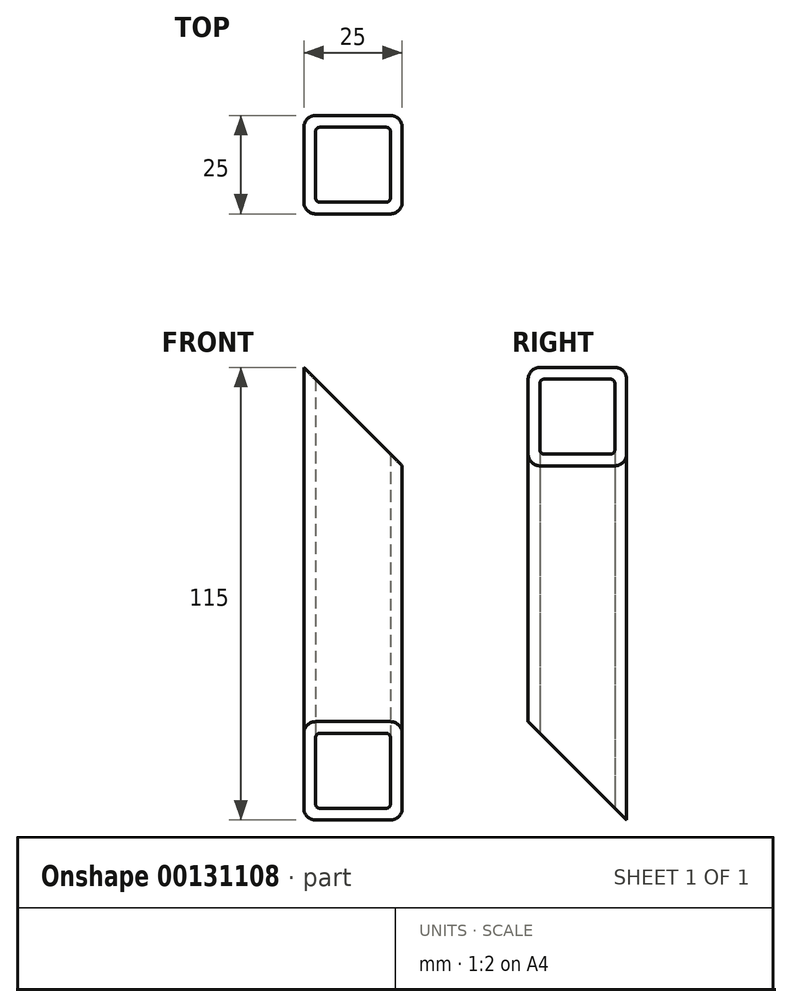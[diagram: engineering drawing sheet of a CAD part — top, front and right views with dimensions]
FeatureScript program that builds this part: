
annotation { "Feature Type Name" : "Feature", "Feature Type Description" : "" }
export const myFeature = defineFeature(function(context is Context, id is Id, definition is map)
    precondition{}
    {
        {
            var Q0;
            Q0=qCreatedBy(makeId("Top.planeOp"),FACE);
            var sketch = newSketch(context, id + "F0", { "sketchPlane" : qUnion([Q0])});
            skLineSegment(sketch, "E0.bottom", {"start": v(12.5, -12.5) * mm, "end": v(-12.5, -12.5) * mm});
            skLineSegment(sketch, "E0.top", {"start": v(12.5, 12.5) * mm, "end": v(-12.5, 12.5) * mm});
            skLineSegment(sketch, "E0.left", {"start": v(12.5, -12.5) * mm, "end": v(12.5, 12.5) * mm});
            skLineSegment(sketch, "E0.right", {"start": v(-12.5, -12.5) * mm, "end": v(-12.5, 12.5) * mm});
            skPoint(sketch, "E0.middle", {"position": v(0, 0) * mm});
            skLineSegment(sketch, "E1.bottom", {"start": v(9.5, -9.5) * mm, "end": v(-9.5, -9.5) * mm});
            skLineSegment(sketch, "E1.top", {"start": v(9.5, 9.5) * mm, "end": v(-9.5, 9.5) * mm});
            skLineSegment(sketch, "E1.left", {"start": v(9.5, -9.5) * mm, "end": v(9.5, 9.5) * mm});
            skLineSegment(sketch, "E1.right", {"start": v(-9.5, -9.5) * mm, "end": v(-9.5, 9.5) * mm});
            skSolve(sketch);
        }
        {
            var Q0;
            Q0=makeQuery(id+"F0.imprint","IMPRINT",FACE,{"disambiguationData":[TD([[makeQuery(id+"F0.imprint","IMPRINT",EDGE,{"derivedFrom":sQuery(id+"F0.wireOp",EDGE,"E0.bottom")}),-1.0]])]});
            extrude(context, id + "F1", {"entities" : qUnion([Q0]), "depth" : 120 * mm});
        }
        {
            var Q0;
            Q0=makeQuery(id+"F1.opExtrude","SWEPT_EDGE",EDGE,{"disambiguationData":[OSD([sQuery(id+"F0.wireOp",EDGE,"E1.bottom"),sQuery(id+"F0.wireOp",EDGE,"E1.right")])]});
            var Q1;
            Q1=makeQuery(id+"F1.opExtrude","SWEPT_EDGE",EDGE,{"disambiguationData":[OSD([sQuery(id+"F0.wireOp",EDGE,"E1.top"),sQuery(id+"F0.wireOp",EDGE,"E1.right")])]});
            var Q2;
            Q2=makeQuery(id+"F1.opExtrude","SWEPT_EDGE",EDGE,{"disambiguationData":[OSD([sQuery(id+"F0.wireOp",EDGE,"E1.top"),sQuery(id+"F0.wireOp",EDGE,"E1.left")])]});
            var Q3;
            Q3=makeQuery(id+"F1.opExtrude","SWEPT_EDGE",EDGE,{"disambiguationData":[OSD([sQuery(id+"F0.wireOp",EDGE,"E1.bottom"),sQuery(id+"F0.wireOp",EDGE,"E1.left")])]});
            fillet(context, id + "F2", {"entities" : qUnion([Q0, Q1, Q2, Q3]), "radius" : 1 * mm, "tangentPropagation" : true, "allowEdgeOverflow" : false});
        }
        {
            var Q0;
            Q0=makeQuery(id+"F1.opExtrude","SWEPT_EDGE",EDGE,{"disambiguationData":[OSD([sQuery(id+"F0.wireOp",EDGE,"E0.top"),sQuery(id+"F0.wireOp",EDGE,"E0.right")])]});
            var Q1;
            Q1=makeQuery(id+"F1.opExtrude","SWEPT_EDGE",EDGE,{"disambiguationData":[OSD([sQuery(id+"F0.wireOp",EDGE,"E0.bottom"),sQuery(id+"F0.wireOp",EDGE,"E0.right")])]});
            var Q2;
            Q2=makeQuery(id+"F1.opExtrude","SWEPT_EDGE",EDGE,{"disambiguationData":[OSD([sQuery(id+"F0.wireOp",EDGE,"E0.top"),sQuery(id+"F0.wireOp",EDGE,"E0.left")])]});
            var Q3;
            Q3=makeQuery(id+"F1.opExtrude","SWEPT_EDGE",EDGE,{"disambiguationData":[OSD([sQuery(id+"F0.wireOp",EDGE,"E0.bottom"),sQuery(id+"F0.wireOp",EDGE,"E0.left")])]});
            fillet(context, id + "F3", {"entities" : qUnion([Q0, Q1, Q2, Q3]), "radius" : 3 * mm, "tangentPropagation" : true, "allowEdgeOverflow" : false});
        }
        {
            var Q0;
            Q0=makeQuery(id+"F1.opExtrude","SWEPT_FACE",FACE,{"disambiguationData":[OSD([sQuery(id+"F0.wireOp",EDGE,"E0.bottom")])]});
            var sketch = newSketch(context, id + "F4", { "sketchPlane" : qUnion([Q0])});
            skLineSegment(sketch, "E2", {"start": v(-15, 120) * mm, "end": v(15, 90) * mm});
            skPoint(sketch, "E2.startSnap0", {"position": v(0, 120) * mm});
            skLineSegment(sketch, "E3", {"start": v(15, 90) * mm, "end": v(15, 120) * mm});
            skLineSegment(sketch, "E4", {"start": v(-15, 120) * mm, "end": v(15, 120) * mm});
            skSolve(sketch);
        }
        {
            var Q0;
            {var subQ0=sQuery(id+"F4.wireOp",EDGE,"E2");var subQ1=sQuery(id+"F0.wireOp",EDGE,"E0.bottom");var subQ2=makeQuery(id+"F1.opExtrude","SWEPT_FACE",FACE,{"disambiguationData":[OSD([subQ1])]});var subQ3=makeQuery(id+"F3.opFillet","BLEND_EDGE",EDGE,{"blendedFrom":[makeQuery(id+"F1.opExtrude","SWEPT_EDGE",EDGE,{"disambiguationData":[OSD([subQ1,sQuery(id+"F0.wireOp",EDGE,"E0.right")])]}),subQ2],"blendedInto":[subQ2]});var subQ4=makeQuery(id+"F4.imprint","INTERSECT",VERTEX,{"derivedFrom":[subQ3,subQ0]});Q0=makeQuery(id+"F4.imprint","IMPRINT",FACE,{"disambiguationData":[TD([[makeQuery(id+"F4.imprint","IMPRINT",EDGE,{"disambiguationData":[TD([[subQ4,-1.0]])],"derivedFrom":subQ0}),1.0]])]});}
            var Q1;
            {var subQ0=sQuery(id+"F4.wireOp",EDGE,"E4");var subQ1=sQuery(id+"F4.wireOp",EDGE,"E2");var subQ2=makeQuery(id+"F4.imprint","INTERSECT",VERTEX,{"derivedFrom":[subQ1,subQ0]});Q1=makeQuery(id+"F4.imprint","IMPRINT",FACE,{"disambiguationData":[TD([[makeQuery(id+"F4.imprint","IMPRINT",EDGE,{"disambiguationData":[TD([[subQ2,-1.0]])],"derivedFrom":subQ1}),1.0]])]});}
            var Q2;
            {var subQ0=sQuery(id+"F4.wireOp",EDGE,"E3");Q2=makeQuery(id+"F4.imprint","IMPRINT",FACE,{"disambiguationData":[TD([[makeQuery(id+"F4.imprint","IMPRINT",EDGE,{"derivedFrom":subQ0}),1.0]])]});}
            extrude(context, id + "F5", {"entities" : qUnion([Q0, Q1, Q2]), "operationType" : NewBodyOperationType.REMOVE, "endBound" : BoundingType.THROUGH_ALL, "oppositeDirection" : true, "depth" : 25 * mm});
        }
        {
            var Q0;
            Q0=makeQuery(id+"F1.opExtrude","SWEPT_FACE",FACE,{"disambiguationData":[OSD([sQuery(id+"F0.wireOp",EDGE,"E0.left")])]});
            var sketch = newSketch(context, id + "F6", { "sketchPlane" : qUnion([Q0])});
            skLineSegment(sketch, "E5", {"start": v(15, 0) * mm, "end": v(-15, 30) * mm});
            skLineSegment(sketch, "E6", {"start": v(-15, 30) * mm, "end": v(-15, 0) * mm});
            skLineSegment(sketch, "E7", {"start": v(-15, 0) * mm, "end": v(15, 0) * mm});
            skSolve(sketch);
        }
        {
            var Q0;
            {var subQ0=sQuery(id+"F6.wireOp",EDGE,"E6");Q0=makeQuery(id+"F6.imprint","IMPRINT",FACE,{"disambiguationData":[TD([[makeQuery(id+"F6.imprint","IMPRINT",EDGE,{"derivedFrom":subQ0}),1.0]])]});}
            var Q1;
            {var subQ0=sQuery(id+"F6.wireOp",EDGE,"E5");var subQ1=sQuery(id+"F0.wireOp",EDGE,"E0.left");var subQ2=makeQuery(id+"F1.opExtrude","SWEPT_FACE",FACE,{"disambiguationData":[OSD([subQ1])]});var subQ3=makeQuery(id+"F3.opFillet","BLEND_EDGE",EDGE,{"blendedFrom":[makeQuery(id+"F1.opExtrude","SWEPT_EDGE",EDGE,{"disambiguationData":[OSD([sQuery(id+"F0.wireOp",EDGE,"E0.top"),subQ1])]}),subQ2],"blendedInto":[subQ2]});var subQ4=makeQuery(id+"F6.imprint","INTERSECT",VERTEX,{"derivedFrom":[subQ3,subQ0]});Q1=makeQuery(id+"F6.imprint","IMPRINT",FACE,{"disambiguationData":[TD([[makeQuery(id+"F6.imprint","IMPRINT",EDGE,{"disambiguationData":[TD([[subQ4,-1.0]])],"derivedFrom":subQ0}),1.0]])]});}
            var Q2;
            {var subQ0=sQuery(id+"F6.wireOp",EDGE,"E7");var subQ1=sQuery(id+"F6.wireOp",EDGE,"E5");var subQ2=makeQuery(id+"F6.imprint","INTERSECT",VERTEX,{"derivedFrom":[subQ1,subQ0]});Q2=makeQuery(id+"F6.imprint","IMPRINT",FACE,{"disambiguationData":[TD([[makeQuery(id+"F6.imprint","IMPRINT",EDGE,{"disambiguationData":[TD([[subQ2,-1.0]])],"derivedFrom":subQ1}),1.0]])]});}
            extrude(context, id + "F7", {"entities" : qUnion([Q0, Q1, Q2]), "operationType" : NewBodyOperationType.REMOVE, "endBound" : BoundingType.THROUGH_ALL, "oppositeDirection" : true, "depth" : 25 * mm});
        }
    });
